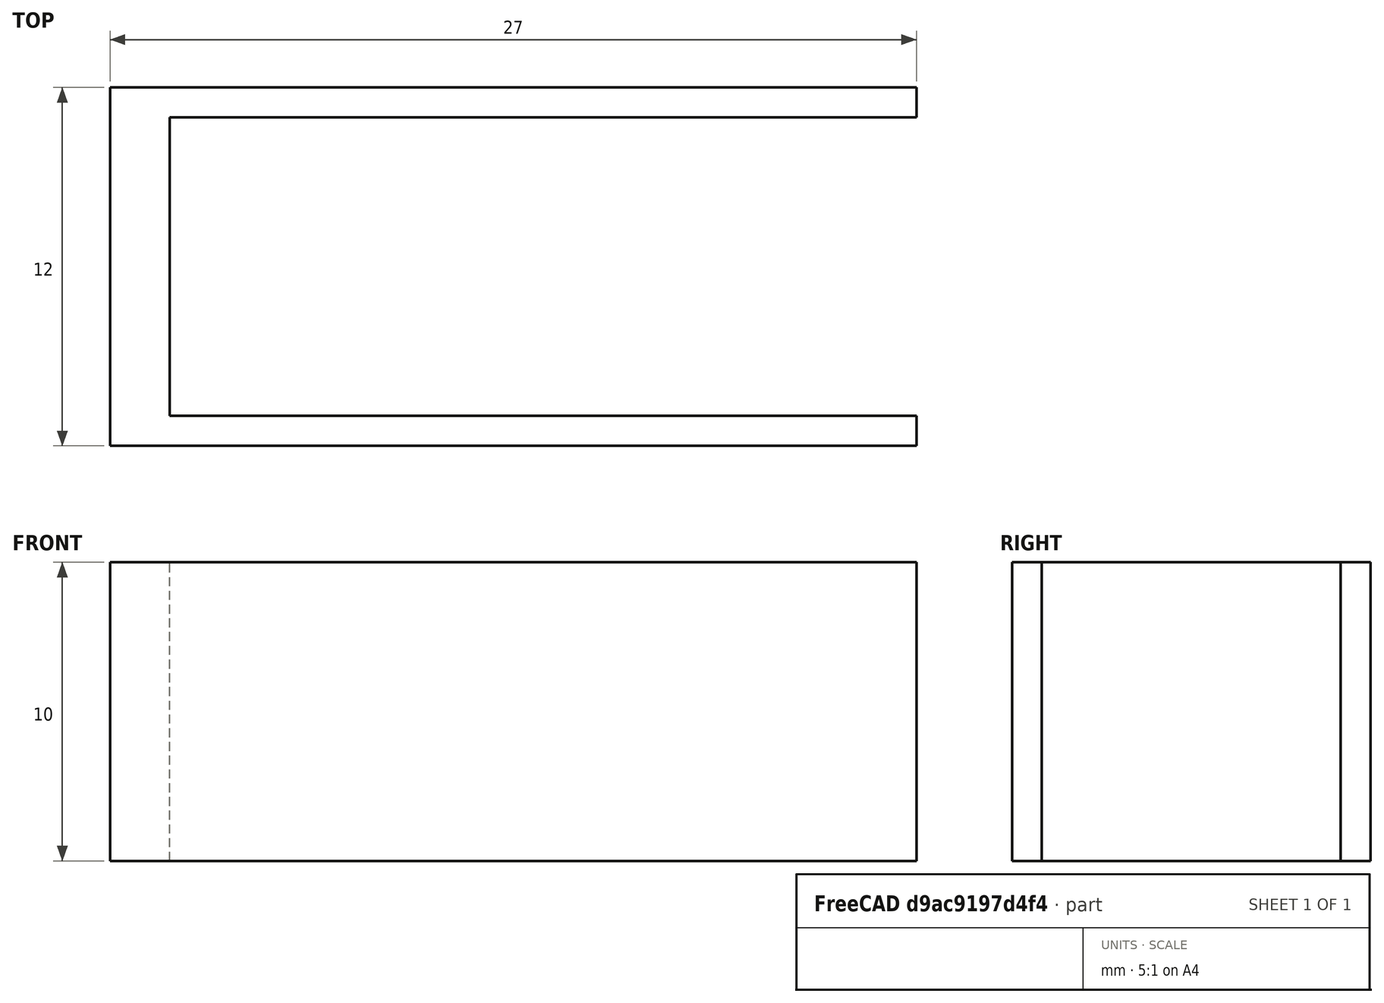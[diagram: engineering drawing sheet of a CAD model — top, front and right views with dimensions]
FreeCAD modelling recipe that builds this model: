
FCSTD DOCUMENT  (FreeCAD 1.0R39109 (Git))
Label: WindowTurnClipReplacement
License: All rights reserved
LicenseURL: http://en.wikipedia.org/wiki/All_rights_reserved
objects: Sketcher::SketchObject×1, PartDesign::Pad×1, PartDesign::Body×1
note: 6 computed .brp shape members not serialized (recipe doc carries the construction recipe); baked Part::Feature solids carry a one-line shape summary decoded from their .brp

FEATURE [Sketcher::SketchObject] Sketch
  ArcFitTolerance = 1e-06
  AttachmentSupport = -> [XY_Plane]
  FullyConstrained = true
  MakeInternals = false
  MapMode = 5
  sketch-geometry (8):
    g0: LineSegment StartX=0 StartY=12 StartZ=0 EndX=0 EndY=0 EndZ=0
    g1: LineSegment StartX=0 StartY=0 StartZ=0 EndX=27 EndY=0 EndZ=0
    g2: LineSegment StartX=27 StartY=12 StartZ=0 EndX=0 EndY=12 EndZ=0
    g3: LineSegment StartX=2 StartY=11 StartZ=0 EndX=2 EndY=1 EndZ=0
    g4: LineSegment StartX=2 StartY=1 StartZ=0 EndX=27 EndY=1 EndZ=0
    g5: LineSegment StartX=27 StartY=11 StartZ=0 EndX=2 EndY=11 EndZ=0
    g6: LineSegment StartX=27 StartY=12 StartZ=0 EndX=27 EndY=11 EndZ=0
    g7: LineSegment StartX=27 StartY=1 StartZ=0 EndX=27 EndY=0 EndZ=0
  constraints (24):
    c: Coincident(g0,g1)
    c: Coincident(g2,g0)
    c: Vertical(g0)
    c: Horizontal(g1)
    c: Horizontal(g2)
    c: PointOnObject(g0,g-2)
    c: PointOnObject(g1,g-1)
    c: Coincident(g3,g4)
    c: Coincident(g5,g3)
    c: Vertical(g3)
    c: Horizontal(g4)
    c: Horizontal(g5)
    c: Coincident(g6,g2)
    c: Coincident(g6,g5)
    c: Coincident(g7,g4)
    c: Coincident(g7,g1)
    c: Vertical(g7)
    c: Vertical(g6)
    c: Equal(g5,g4)
    c: Equal(g6,g7)
    c: DistanceY(g7,g7) = 1
    c: DistanceX(g0,g3) = 2
    c: DistanceX(g5,g5) = 25
    c: DistanceY(g3,g3) = 10
FEATURE [PartDesign::Pad] Pad
  Direction = (0,0,1)
  Length = 10
  Length2 = 10
  Profile = -> Sketch
  ReferenceAxis = -> Sketch [N_Axis]
  Refine = true
  Suppressed = false
  Type = 0
FEATURE [PartDesign::Body] Body
  AllowCompound = false
  Group = -> [Sketch,Pad]
  Origin = -> Origin
  Tip = -> Pad
